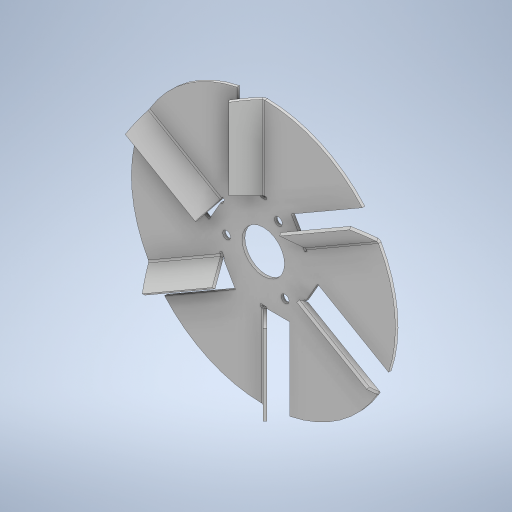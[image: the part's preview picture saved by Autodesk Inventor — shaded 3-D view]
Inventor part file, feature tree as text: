
AUTODESK INVENTOR PART (.ipt)
format: ipt  version: 2024.2 (Build 282272000, 272)  size: 621,056 bytes
history: native  units: mm
features: sketch x4, sheet_metal_op x2, pattern_circular x2, other x2, extrude x1, hole x1, projected_geometry x1
ambient origin geometry x8: Origin, YZ Plane, XZ Plane, XY Plane, X Axis, Y Axis, Z Axis, Center Point
bodies: Solid1 (feature_tree)
feature tree (13):
  sheet_metal_op  "Face1"
  extrude  "Extrusion1"  Depth=200.0mm
  sheet_metal_op  "Fold1"
  pattern_circular  "Circular Pattern1"  Count=20  [1 undecoded]
  sketch  "Sketch4"  dims[d7=32.0mm d8=36.0mm d9=0.0mm d10=0.0mm d11=2.0mm d12=1.0mm d13=4.0mm d14=2.0mm d15=45.0deg d16=2.0mm d17=60.0mm d18=360.0deg d21=6.0mm d22=6.0mm d23=4.0mm d24=2.0mm d25=90.0deg d26=2.0mm d27=20.594885mm d28=30.0mm d29=360.0deg d32=28.0mm d33=1.047198mm]
  hole  "Hole1"  [1 undecoded]
  pattern_circular  "Circular Pattern2"  Count=2  [1 undecoded]
  sketch  "Sketch1"  dims[d0=32.1mm d1=200.0mm]
  other  "Plate1"
  sketch  "Sketch2"  dims[d2=2.0mm d3=200.0mm]
  sketch  "Sketch3"  dims[d4=1.0mm d5=1.0mm d6=20.0mm]
  projected_geometry  "Projected Loop1"
  other  "Definition1"
note: 3 required parameter values undecoded (feature->parameter linkage not recoverable at this tier; creation-order binding heuristic only, values carry confidence <= 0.55)
